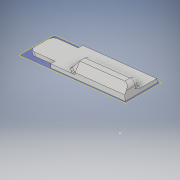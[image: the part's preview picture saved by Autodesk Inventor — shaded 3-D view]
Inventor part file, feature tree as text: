
AUTODESK INVENTOR PART (.ipt)
format: ipt  version: 2017 (Build 210142000, 142)  size: 279,040 bytes
history: native  units: in
note: dims shown in document units (in); Inventor stores cm internally (conversion verified against a paired STEP export)
features: sketch x10, extrude x6, fillet x5, plane x2, sweep x1, shell x1, loft x1, split x1, other x1
ambient origin geometry x8: Origin, YZ Plane, XZ Plane, XY Plane, X Axis, Y Axis, Z Axis, Center Point
bodies: Solid1 (feature_tree)
feature tree (28):
  sweep  "Sweep1"
  shell  "Shell1"  Thickness=0.0in
  extrude  "Extrusion1"  Depth=0.5118in
  extrude  "Extrusion2"  Depth=0.0984in
  fillet  "Fillet1"  Radius=0.0787in
  plane  "Work Plane1"
  loft  "Loft1"
  fillet  "Fillet2"  Radius=0.0984in
  fillet  "Fillet3"  Radius=0.1969in
  fillet  "Fillet4"  [1 undecoded]
  sketch  "Sketch6"  dims[d26=0.0394in d27=0.0394in]
  extrude  "Extrusion3"  Depth=0.0394in
  extrude  "Extrusion4"  Depth=0.0394in
  extrude  "Extrusion5"  Depth=0.0591in TaperAngle=0.0deg
  fillet  "Fillet5"  Radius=0.0591in
  plane  "Work Plane2"
  split  "Split1"
  extrude  "Extrusion7"  Depth=0.0787in
  sketch  "Sketch1"  dims[d0=1.6732in d1=0.7087in d4=0.0in d5=0.0in]
  sketch  "Sketch2"  dims[d6=0.0591in d8=0.5118in]
  sketch  "Sketch3"  dims[d9=90.0deg d10=0.0984in d11=0.0787in d12=0.0in]
  sketch  "Sketch4"  dims[d16=0.0394in d17=1.1024in d18=0.0in d19=0.0984in d20=0.1969in d21=0.0in d22=90.0deg]
  sketch  "Sketch5"  dims[d23=0.0in d24=90.0deg d25=0.0394in]
  other  "Edges1"
  sketch  "Sketch7"  dims[d28=0.0591in d29=0.0in d30=0.0591in d31=0.0in d32=0.0591in]
  sketch  "Sketch8"  dims[d33=0.1575in d34=0.0787in]
  sketch  "Sketch9"  dims[d35=0.1575in d36=0.0in]
  sketch  "Sketch11"  dims[d37=0.0787in d41=0.0in d44=0.1181in d45=0.1181in d46=0.3937in d47=0.0in]
note: 1 required parameter value undecoded (feature->parameter linkage not recoverable at this tier; creation-order binding heuristic only, values carry confidence <= 0.55)
